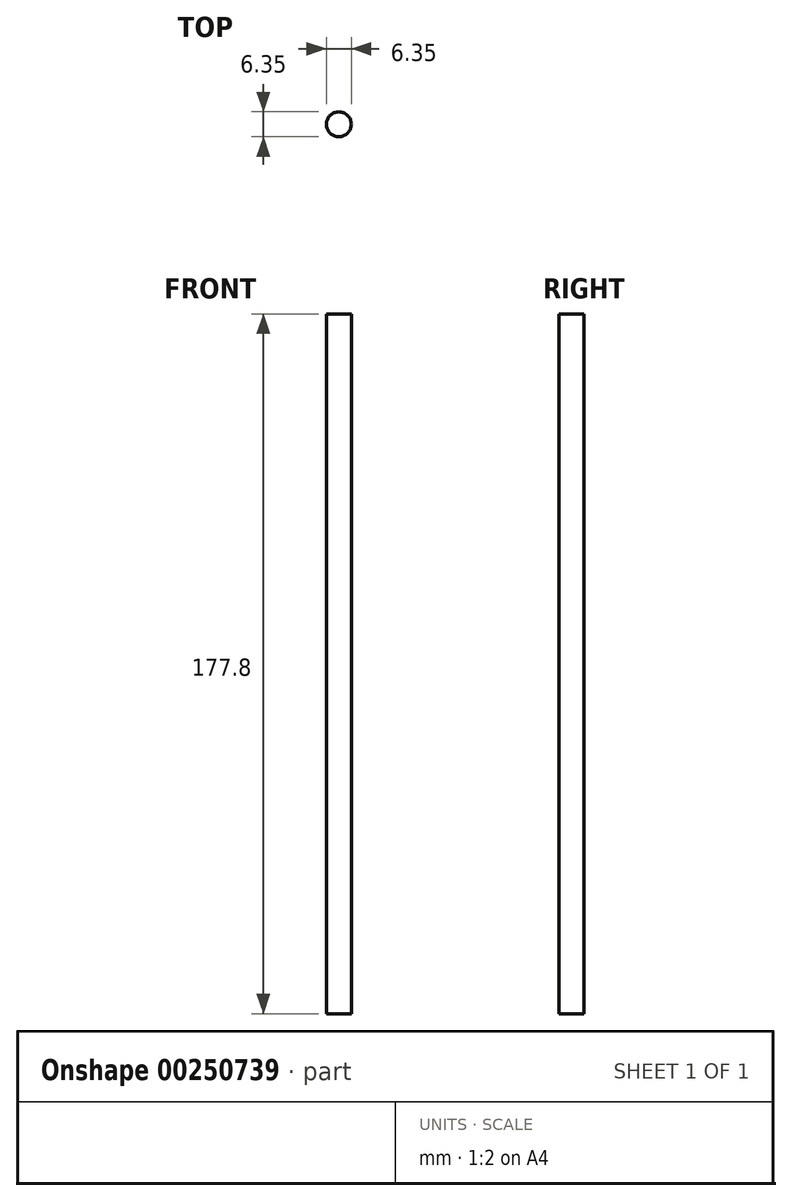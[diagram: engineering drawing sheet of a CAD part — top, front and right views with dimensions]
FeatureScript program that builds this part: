
annotation { "Feature Type Name" : "Feature", "Feature Type Description" : "" }
export const myFeature = defineFeature(function(context is Context, id is Id, definition is map)
    precondition{}
    {
        {
            var Q0;
            Q0=qCreatedBy(makeId("Top.planeOp"),FACE);
            var sketch = newSketch(context, id + "F0", { "sketchPlane" : qUnion([Q0])});
            skCircle(sketch, "E0", {"center": v(-45.5, 14.45) * mm, "radius": 3.18 * mm});
            skSolve(sketch);
        }
        {
            var Q0;
            Q0 = qSketchRegion(id + "F0", true);
            extrude(context, id + "F1", {"entities" : qUnion([Q0]), "depth" : 177.8 * mm});
        }
    });
